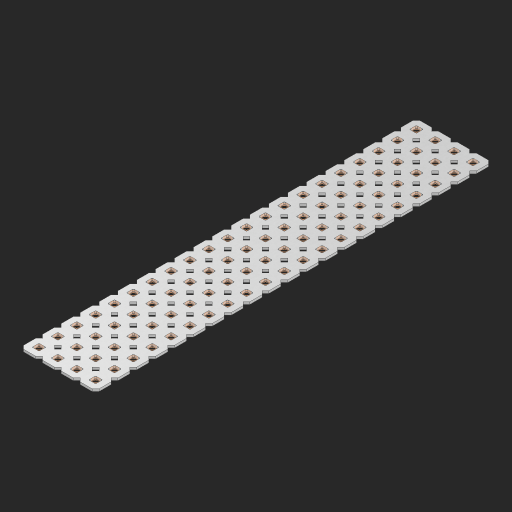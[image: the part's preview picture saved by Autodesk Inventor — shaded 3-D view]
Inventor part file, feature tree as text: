
AUTODESK INVENTOR PART (.ipt)
format: ipt  version: 2023 (Build 270158000, 158)  size: 1,250,816 bytes
history: native  units: in
note: dims shown in document units (in); Inventor stores cm internally (conversion verified against a paired STEP export)
features: other x85, extrude x83, sketch x2, pattern_linear x1
ambient origin geometry x8: Origin, YZ Plane, XZ Plane, XY Plane, X Axis, Y Axis, Z Axis, Center Point
bodies: Solid1 (feature_tree), Body (feature_tree)
feature tree (171):
  pattern_linear  "Rectangular Pattern1"  Spacing1=0.09in  [1 undecoded]
  sketch  "Sketch1"  dims[d1=0.5in]
  sketch  "Sketch2"  dims[d2=0.182in d3=0.09in d4=0.09in d5=0.09in d6=0.09in d7=0.09in d8=0.09in d9=0.09in d10=0.09in d11=0.02in d13=0.0in d14=0.172in d15=0.0625in d16=0.0in d19=0.5in d22=0.5in]
  other  "Srf1"
  other  "Srf126"
  other  "Srf127"
  other  "Srf128"
  other  "Srf129"
  other  "Srf130"
  other  "Srf131"
  other  "Srf250"
  other  "Srf251"
  other  "Srf252"
  other  "Srf253"
  other  "Srf254"
  other  "Srf255"
  other  "Srf256"
  other  "Srf257"
  other  "Srf258"
  other  "Srf259"
  other  "Srf260"
  other  "Srf261"
  other  "Srf262"
  other  "Srf263"
  other  "Srf268"
  other  "Srf269"
  other  "Srf270"
  other  "Srf271"
  other  "Srf272"
  other  "Srf273"
  other  "Srf274"
  other  "Srf275"
  other  "Srf276"
  other  "Srf277"
  other  "Srf278"
  other  "Srf279"
  other  "Srf280"
  other  "Srf281"
  other  "Srf282"
  other  "Srf283"
  other  "Srf284"
  other  "Srf285"
  other  "Srf286"
  other  "Srf287"
  other  "Srf288"
  other  "Srf293"
  other  "Srf294"
  other  "Srf295"
  other  "Srf296"
  other  "Srf297"
  other  "Srf298"
  other  "Srf299"
  other  "Srf300"
  other  "Srf301"
  other  "Srf302"
  other  "Srf303"
  other  "Srf304"
  other  "Srf305"
  other  "Srf306"
  other  "Srf307"
  other  "Srf308"
  other  "Srf309"
  other  "Srf310"
  other  "Srf311"
  other  "Srf312"
  other  "Srf313"
  other  "Srf318"
  other  "Srf319"
  other  "Srf320"
  other  "Srf321"
  other  "Srf322"
  other  "Srf323"
  other  "Srf324"
  other  "Srf325"
  other  "Srf326"
  other  "Srf327"
  other  "Srf328"
  other  "Srf329"
  other  "Srf330"
  other  "Srf331"
  other  "Srf332"
  other  "Srf333"
  other  "Srf334"
  other  "Srf335"
  other  "Srf336"
  other  "Srf337"
  other  "Srf338"
  other  "Circle"
  extrude  "ExtrusionSrf126"  Depth=0.09in
  extrude  "ExtrusionSrf127"  Depth=0.09in
  extrude  "ExtrusionSrf128"  Depth=0.09in
  extrude  "ExtrusionSrf129"  Depth=0.09in
  extrude  "ExtrusionSrf130"  Depth=0.09in
  extrude  "ExtrusionSrf131"  Depth=0.09in
  extrude  "ExtrusionSrf250"  Depth=0.09in
  extrude  "ExtrusionSrf251"  Depth=0.02in
  extrude  "ExtrusionSrf252"  TaperAngle=0.0deg  [1 undecoded]
  extrude  "ExtrusionSrf253"  Depth=0.5in
  extrude  "ExtrusionSrf254"  Depth=0.0625in TaperAngle=0.0deg
  extrude  "ExtrusionSrf255"  Depth=0.5in
  extrude  "ExtrusionSrf256"  Depth=0.5in
  extrude  "ExtrusionSrf257"  [1 undecoded]
  extrude  "ExtrusionSrf258"  [1 undecoded]
  extrude  "ExtrusionSrf259"  [1 undecoded]
  extrude  "ExtrusionSrf260"  [1 undecoded]
  extrude  "ExtrusionSrf261"  [1 undecoded]
  extrude  "ExtrusionSrf262"  [1 undecoded]
  extrude  "ExtrusionSrf263"  [1 undecoded]
  extrude  "ExtrusionSrf268"  [1 undecoded]
  extrude  "ExtrusionSrf269"  [1 undecoded]
  extrude  "ExtrusionSrf270"  [1 undecoded]
  extrude  "ExtrusionSrf271"  [1 undecoded]
  extrude  "ExtrusionSrf272"  [1 undecoded]
  extrude  "ExtrusionSrf273"  [1 undecoded]
  extrude  "ExtrusionSrf274"  [1 undecoded]
  extrude  "ExtrusionSrf275"  [1 undecoded]
  extrude  "ExtrusionSrf276"  [1 undecoded]
  extrude  "ExtrusionSrf277"  [1 undecoded]
  extrude  "ExtrusionSrf278"  [1 undecoded]
  extrude  "ExtrusionSrf279"  [1 undecoded]
  extrude  "ExtrusionSrf280"  [1 undecoded]
  extrude  "ExtrusionSrf281"  [1 undecoded]
  extrude  "ExtrusionSrf282"  [1 undecoded]
  extrude  "ExtrusionSrf283"  [1 undecoded]
  extrude  "ExtrusionSrf284"  [1 undecoded]
  extrude  "ExtrusionSrf285"  [1 undecoded]
  extrude  "ExtrusionSrf286"  [1 undecoded]
  extrude  "ExtrusionSrf287"  [1 undecoded]
  extrude  "ExtrusionSrf288"  [1 undecoded]
  extrude  "ExtrusionSrf293"  [1 undecoded]
  extrude  "ExtrusionSrf294"  [1 undecoded]
  extrude  "ExtrusionSrf295"  [1 undecoded]
  extrude  "ExtrusionSrf296"  [1 undecoded]
  extrude  "ExtrusionSrf297"  [1 undecoded]
  extrude  "ExtrusionSrf298"  [1 undecoded]
  extrude  "ExtrusionSrf299"  [1 undecoded]
  extrude  "ExtrusionSrf300"  [1 undecoded]
  extrude  "ExtrusionSrf301"  [1 undecoded]
  extrude  "ExtrusionSrf302"  [1 undecoded]
  extrude  "ExtrusionSrf303"  [1 undecoded]
  extrude  "ExtrusionSrf304"  [1 undecoded]
  extrude  "ExtrusionSrf305"  [1 undecoded]
  extrude  "ExtrusionSrf306"  [1 undecoded]
  extrude  "ExtrusionSrf307"  [1 undecoded]
  extrude  "ExtrusionSrf308"  [1 undecoded]
  extrude  "ExtrusionSrf309"  [1 undecoded]
  extrude  "ExtrusionSrf310"  [1 undecoded]
  extrude  "ExtrusionSrf311"  [1 undecoded]
  extrude  "ExtrusionSrf312"  [1 undecoded]
  extrude  "ExtrusionSrf313"  [1 undecoded]
  extrude  "ExtrusionSrf318"  [1 undecoded]
  extrude  "ExtrusionSrf319"  [1 undecoded]
  extrude  "ExtrusionSrf320"  [1 undecoded]
  extrude  "ExtrusionSrf321"  [1 undecoded]
  extrude  "ExtrusionSrf322"  [1 undecoded]
  extrude  "ExtrusionSrf323"  [1 undecoded]
  extrude  "ExtrusionSrf324"  [1 undecoded]
  extrude  "ExtrusionSrf325"  [1 undecoded]
  extrude  "ExtrusionSrf326"  [1 undecoded]
  extrude  "ExtrusionSrf327"  [1 undecoded]
  extrude  "ExtrusionSrf328"  [1 undecoded]
  extrude  "ExtrusionSrf329"  [1 undecoded]
  extrude  "ExtrusionSrf330"  [1 undecoded]
  extrude  "ExtrusionSrf331"  [1 undecoded]
  extrude  "ExtrusionSrf332"  [1 undecoded]
  extrude  "ExtrusionSrf333"  [1 undecoded]
  extrude  "ExtrusionSrf334"  [1 undecoded]
  extrude  "ExtrusionSrf335"  [1 undecoded]
  extrude  "ExtrusionSrf336"  [1 undecoded]
  extrude  "ExtrusionSrf337"  [1 undecoded]
  extrude  "ExtrusionSrf338"  [1 undecoded]
note: 72 required parameter values undecoded (feature->parameter linkage not recoverable at this tier; creation-order binding heuristic only, values carry confidence <= 0.55)
